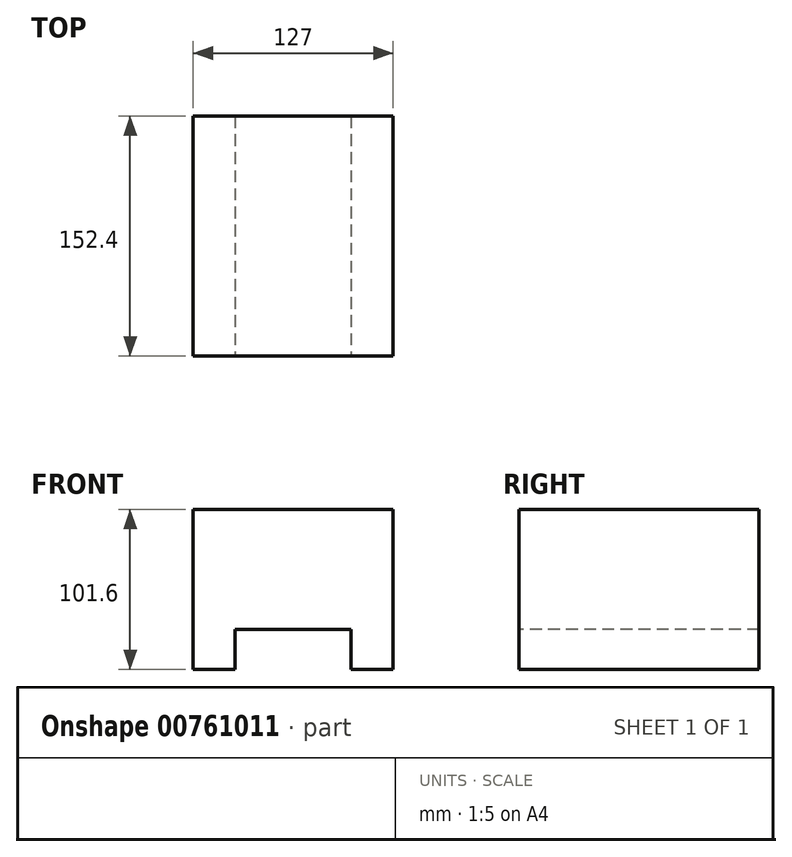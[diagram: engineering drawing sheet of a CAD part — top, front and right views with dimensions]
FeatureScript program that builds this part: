
annotation { "Feature Type Name" : "Feature", "Feature Type Description" : "" }
export const myFeature = defineFeature(function(context is Context, id is Id, definition is map)
    precondition{}
    {
        {
            var Q0;
            Q0=qCreatedBy(makeId("Top.planeOp"),FACE);
            var sketch = newSketch(context, id + "F0", { "sketchPlane" : qUnion([Q0])});
            skLineSegment(sketch, "E0.bottom", {"start": v(63.5, 76.2) * mm, "end": v(-63.5, 76.2) * mm});
            skLineSegment(sketch, "E0.top", {"start": v(63.5, -76.2) * mm, "end": v(-63.5, -76.2) * mm});
            skLineSegment(sketch, "E0.left", {"start": v(63.5, 76.2) * mm, "end": v(63.5, -76.2) * mm});
            skLineSegment(sketch, "E0.right", {"start": v(-63.5, 76.2) * mm, "end": v(-63.5, -76.2) * mm});
            skPoint(sketch, "E0.middle", {"position": v(0, 0) * mm});
            skSolve(sketch);
        }
        {
            var Q0;
            Q0=makeQuery(id+"F0.imprint","IMPRINT",FACE,{"disambiguationData":[TD([[makeQuery(id+"F0.imprint","IMPRINT",EDGE,{"derivedFrom":sQuery(id+"F0.wireOp",EDGE,"E0.bottom")}),1.0]])]});
            extrude(context, id + "F1", {"entities" : qUnion([Q0]), "depth" : 101.6 * mm, "offsetDistance" : 25.4 * mm});
        }
        {
            var Q0;
            Q0=qCreatedBy(makeId("Front.planeOp"),FACE);
            var sketch = newSketch(context, id + "F2", { "sketchPlane" : qUnion([Q0])});
            skLineSegment(sketch, "E1.bottom", {"start": v(36.86, 25.4) * mm, "end": v(-36.86, 25.4) * mm});
            skLineSegment(sketch, "E1.top", {"start": v(36.86, -25.4) * mm, "end": v(-36.86, -25.4) * mm});
            skLineSegment(sketch, "E1.left", {"start": v(36.86, 25.4) * mm, "end": v(36.86, -25.4) * mm});
            skLineSegment(sketch, "E1.right", {"start": v(-36.86, 25.4) * mm, "end": v(-36.86, -25.4) * mm});
            skPoint(sketch, "E1.middle", {"position": v(0, 0) * mm});
            skSolve(sketch);
        }
        {
            var Q0;
            Q0=makeQuery(id+"F2.imprint","IMPRINT",FACE,{"disambiguationData":[TD([[makeQuery(id+"F2.imprint","IMPRINT",EDGE,{"derivedFrom":sQuery(id+"F2.wireOp",EDGE,"E1.bottom")}),1.0]])]});
            extrude(context, id + "F3", {"entities" : qUnion([Q0]), "operationType" : NewBodyOperationType.REMOVE, "endBound" : BoundingType.SYMMETRIC, "oppositeDirection" : true, "depth" : 5080 * mm, "offsetDistance" : 25.4 * mm});
        }
    });
